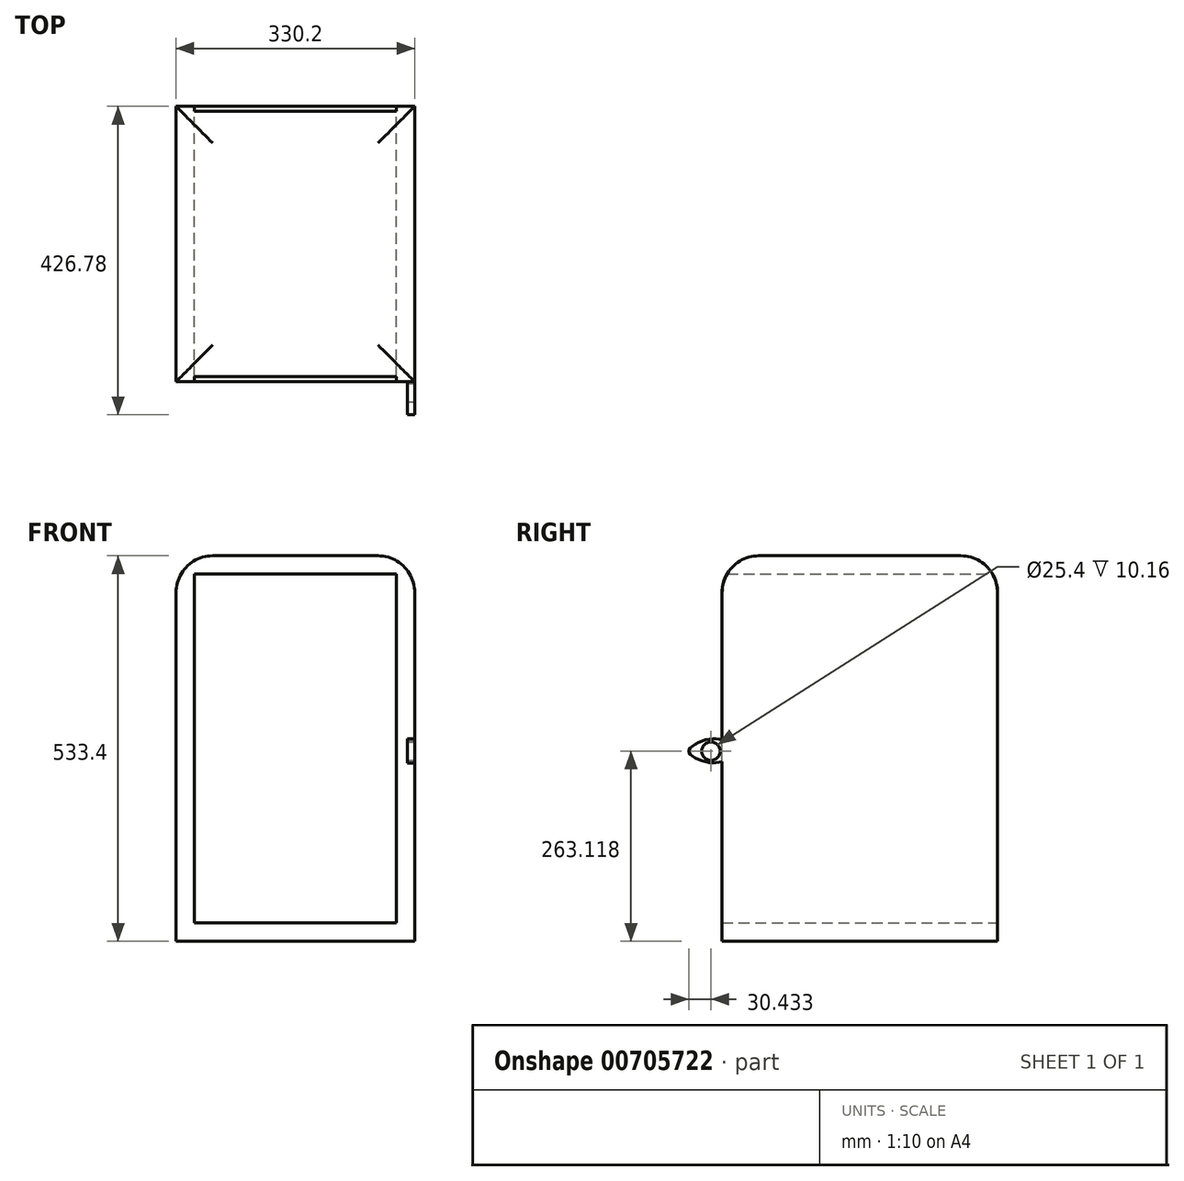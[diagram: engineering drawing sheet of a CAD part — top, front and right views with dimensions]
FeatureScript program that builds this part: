
annotation { "Feature Type Name" : "Feature", "Feature Type Description" : "" }
export const myFeature = defineFeature(function(context is Context, id is Id, definition is map)
    precondition{}
    {
        {
            var Q0;
            Q0=qCreatedBy(makeId("Front.planeOp"),FACE);
            var sketch = newSketch(context, id + "F0", { "sketchPlane" : qUnion([Q0])});
            skPoint(sketch, "E0.middle", {"position": v(0, 0) * mm});
            skLineSegment(sketch, "E1.bottom", {"start": v(139.7, -241.3) * mm, "end": v(-139.7, -241.3) * mm});
            skLineSegment(sketch, "E1.top", {"start": v(139.7, 241.3) * mm, "end": v(-139.7, 241.3) * mm});
            skLineSegment(sketch, "E1.left", {"start": v(139.7, -241.3) * mm, "end": v(139.7, 241.3) * mm});
            skLineSegment(sketch, "E1.right", {"start": v(-139.7, -241.3) * mm, "end": v(-139.7, 241.3) * mm});
            skLineSegment(sketch, "E2.bottom", {"start": v(165.1, -266.7) * mm, "end": v(-165.1, -266.7) * mm});
            skLineSegment(sketch, "E2.top", {"start": v(165.1, 266.7) * mm, "end": v(-165.1, 266.7) * mm});
            skLineSegment(sketch, "E2.left", {"start": v(165.1, -266.7) * mm, "end": v(165.1, 266.7) * mm});
            skLineSegment(sketch, "E2.right", {"start": v(-165.1, -266.7) * mm, "end": v(-165.1, 266.7) * mm});
            skSolve(sketch);
        }
        {
            var Q0;
            Q0 = qSketchRegion(id + "F0", true);
            extrude(context, id + "F1", {"entities" : qUnion([Q0]), "depth" : 381 * mm, "offsetDistance" : 25.4 * mm});
        }
        {
            var Q0;
            Q0=makeQuery(id+"F1.opExtrude","SWEPT_FACE",FACE,{"disambiguationData":[OSD([sQuery(id+"F0.wireOp",EDGE,"E2.left")])]});
            var sketch = newSketch(context, id + "F2", { "sketchPlane" : qUnion([Q0])});
            skPoint(sketch, "E3.centerSnap0", {"position": v(-381, 0) * mm});
            skFitSpline(sketch, "E4", {"points": [v(-378.22, 10.45) * mm, v(-406.68, 11.22) * mm, v(-426.78, -3.58) * mm, v(-406.68, -17.62) * mm, v(-378.22, -16.86) * mm, v(-367.62, -3.58) * mm, v(-378.22, 10.45) * mm]});
            skCircle(sketch, "E5", {"center": v(-396.35, -3.58) * mm, "radius": 12.7 * mm});
            skSolve(sketch);
        }
        {
            var Q0;
            Q0 = qSketchRegion(id + "F2", true);
            extrude(context, id + "F3", {"entities" : qUnion([Q0]), "operationType" : NewBodyOperationType.ADD, "oppositeDirection" : true, "depth" : 10.16 * mm, "offsetDistance" : 25.4 * mm});
        }
        {
            var Q0;
            Q0=makeQuery(id+"F1.opExtrude","SWEPT_FACE",FACE,{"disambiguationData":[OSD([sQuery(id+"F0.wireOp",EDGE,"E2.top")])]});
            fillet(context, id + "F4", {"entities" : qUnion([Q0]), "radius" : 50.8 * mm, "tangentPropagation" : true, "allowEdgeOverflow" : false});
        }
    });
